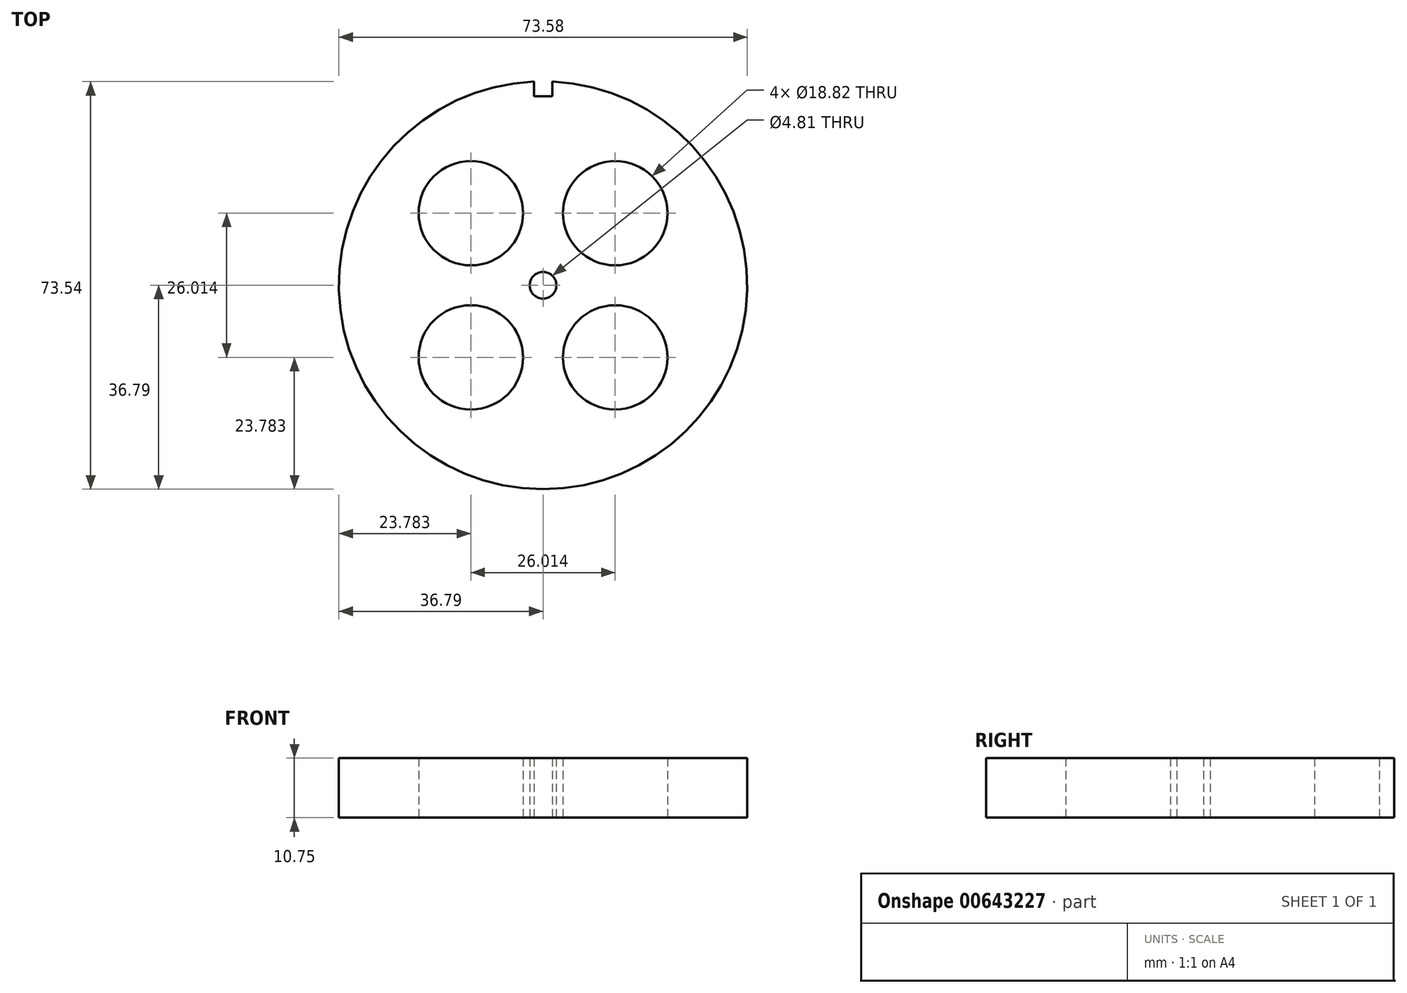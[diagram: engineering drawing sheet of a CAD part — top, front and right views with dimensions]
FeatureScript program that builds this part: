
annotation { "Feature Type Name" : "Feature", "Feature Type Description" : "" }
export const myFeature = defineFeature(function(context is Context, id is Id, definition is map)
    precondition{}
    {
        {
            var Q0;
            Q0=qCreatedBy(makeId("Top.planeOp"),FACE);
            var sketch = newSketch(context, id + "F0", { "sketchPlane" : qUnion([Q0])});
            skCircle(sketch, "E0", {"center": v(0, 0) * mm, "radius": 36.8 * mm});
            skLineSegment(sketch, "E1", {"start": v(0, 0) * mm, "end": v(-36.8, 0) * mm, "construction": true});
            skLineSegment(sketch, "E2", {"start": v(0, 0) * mm, "end": v(0, 36.8) * mm, "construction": true});
            skLineSegment(sketch, "E3", {"start": v(-18.4, 0) * mm, "end": v(0, 18.4) * mm, "construction": true});
            skLineSegment(sketch, "E4", {"start": v(0, 0) * mm, "end": v(-26.01, 26.01) * mm, "construction": true});
            skCircle(sketch, "E5", {"center": v(-13, 13) * mm, "radius": 9.4 * mm});
            skCircle(sketch, "E6.1.0", {"center": v(-13, -13) * mm, "radius": 9.4 * mm});
            skCircle(sketch, "E6.2.0", {"center": v(13, -13) * mm, "radius": 9.4 * mm});
            skCircle(sketch, "E6.3.0", {"center": v(13, 13) * mm, "radius": 9.4 * mm});
            skCircle(sketch, "E7", {"center": v(0, 0) * mm, "radius": 2.4 * mm});
            skPoint(sketch, "E8", {"position": v(0, 34.1) * mm});
            skLineSegment(sketch, "E9", {"start": v(0, 34.1) * mm, "end": v(1.65, 34.1) * mm});
            skLineSegment(sketch, "E10", {"start": v(1.65, 34.1) * mm, "end": v(1.65, 36.75) * mm});
            skLineSegment(sketch, "E11.MirrorCS", {"start": v(-1.65, 34.1) * mm, "end": v(-1.65, 36.75) * mm});
            skLineSegment(sketch, "E12.MirrorCS", {"start": v(0, 34.1) * mm, "end": v(-1.65, 34.1) * mm});
            skSolve(sketch);
        }
        {
            var Q0;
            Q0=makeQuery(id+"F0.imprint","IMPRINT",FACE,{"disambiguationData":[TD([[makeQuery(id+"F0.imprint","IMPRINT",EDGE,{"derivedFrom":sQuery(id+"F0.wireOp",EDGE,"E5")}),-1.0]])]});
            extrude(context, id + "F1", {"entities" : qUnion([Q0]), "depth" : 10.75 * mm, "offsetDistance" : 25 * mm});
        }
    });
